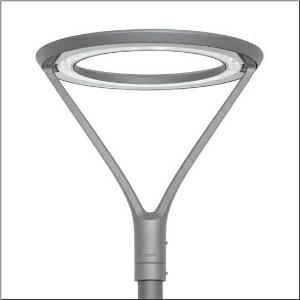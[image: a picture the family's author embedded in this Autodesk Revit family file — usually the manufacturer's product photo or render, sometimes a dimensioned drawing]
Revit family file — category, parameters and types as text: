
# Revit family: dl_20___st1_2a_5xa512832a008p_2471
name_source: partatom
category: Lighting Fixtures
units: mm (PartAtom-declared; Revit-internal decimal feet)

## family parameters
Cut with Voids When Loaded = No
Host = Face
Light Source = No
Part Type = Normal
Room Calculation Point = No
Round Connector Dimension = Use Diameter
Shared = No

## types (1)
- --- (1 x LED, 4200 lm, 43.6 W, 2200K)
    Apparent Load = 44 VA
    CIE Flux Codes = 32 72 97 100 100
    Color Rendering = 70
    Color Temperature = 2200K
    Default Elevation = 1800 mm
    Description = DL® 20, mast luminaire, primary light control with reflector, highly specular, primary optical cover: cover, of toughened safety glass of clear glass with excellent transmission level, light distribution: ST1.2a, light emission: direct distribution, primary light characteristic: asymmetric, installation type: post-top, LED, High Power LED, rated luminous flux: 4.180lm, luminous efficacy: 79lm/W, light colour: 722, colour temperature: 2200K, control gear: Plus, control: flexible luminous flux parameterisation, time-dependent luminous flux control, constant luminous flux control, digital communication interface, power reduction, overheat protection, electronic power reduction, mains connection: 230..240V, 50/60Hz, connection cable pre-assembled, cable length: 5m, start of lifetime: 53W, end of service life: 54W, reduction: 24W, luminaire housing, upper part, of cast aluminium, powder-coated, Siteco® metallic grey (DB 702S), diameter: 690mm, height: 690mm, spigot size: 76mm (post-top), mounting height: 4..6m, luminaire housing, of cast aluminium, powder-coated, Siteco® metallic grey (DB 702S), equipment: Power, protection rating (complete): IP66, insulation class (complete): insulation class II (safety insulation), certification: CE, ENEC, VDE, impact resistance: IK08, permissible operating ambient temperature: -25..+30°C, standard-compliant lighting for roads and squares, packaging unit: 1 piece

Light Distribution: ST1.2a
    Height = 690 mm
    Lamp = 1 x LED
    Lamp Light Flux = 4200 lm
    Lamp Power = 43.6 W
    Lamp count = 1
    Length = 690 mm
    Luminous efficacy = 96 lm/W
    Manufacturer = Siteco
    ModVariant = No
    Model = 5XA512832A008P
    Number of Poles = 1
    OnlyDefault = Yes
    Power Factor = 1
    Product Name = DL 20 | ST1.2a
    Product group = mast luminaire | pylon top
    ProductGroupID = 6100
    Protection Class = Protection class II
    Protection Degree = IP 66
    RLX_Detail_Level = 1
    RLX_Emergency_Light_Flux = 0 lm
    RLX_Emergency_Type = 0
    RLX_Emergency_Type_DB = No
    RlxData = <blob elided: 207069 chars, md5=1bbbcc19>
    Socket = socket
    Standby Power = 0 W
    System Light Flux = 4200 lm
    System Power = 44 W
    Type Comments = factory setting: luminous flux: 100 % | dim-lin: 254 | 587 mA
    Type Image = l_1006001.jpg
    URL = http://relux.com
    VarID = @adj_085229
    Voltage = 0 V
    Weight = 0.00 kg
    Width = 0 mm  [stored 0 ft]

note: [stored X ft] marks values corroborated as IEEE doubles in the binary element streams (Revit-internal decimal feet)

## geometry (parser evidence)
native form markers: Blend x4, Sweep x9
no freeform markers — native parametric forms only
